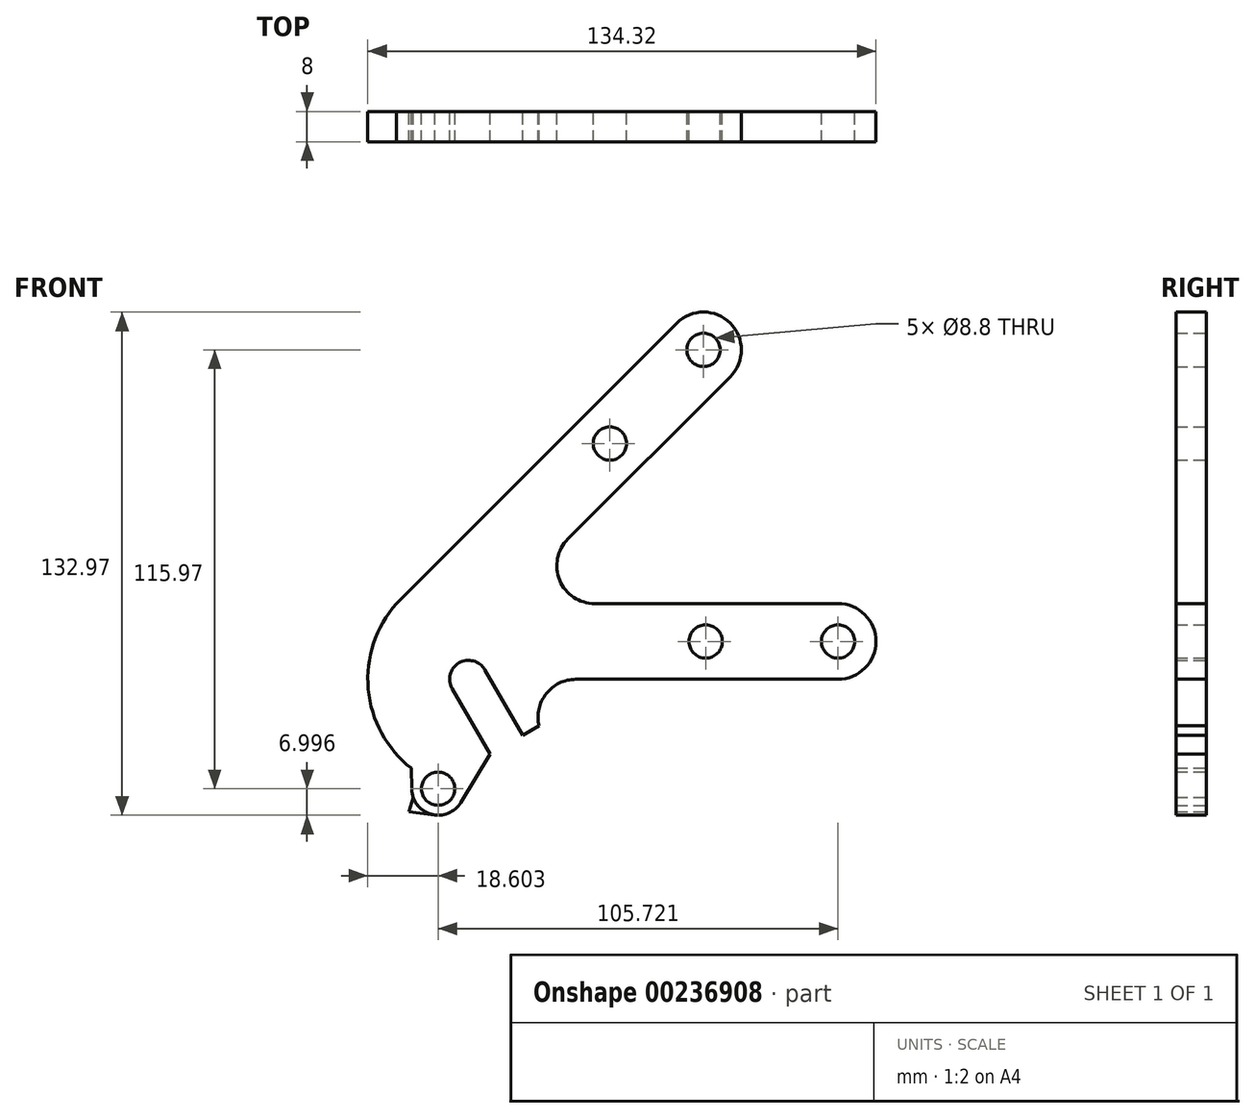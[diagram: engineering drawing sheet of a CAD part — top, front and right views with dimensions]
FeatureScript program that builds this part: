
annotation { "Feature Type Name" : "Feature", "Feature Type Description" : "" }
export const myFeature = defineFeature(function(context is Context, id is Id, definition is map)
    precondition{}
    {
        {
            var Q0;
            Q0=qCreatedBy(makeId("Front.planeOp"),FACE);
            var sketch = newSketch(context, id + "F0", { "sketchPlane" : qUnion([Q0])});
            skLineSegment(sketch, "E0", {"start": v(-20.18, 0) * mm, "end": v(-273.76, 0) * mm, "construction": true});
            skLineSegment(sketch, "E1", {"start": v(-273.76, 0) * mm, "end": v(-273.76, 78.06) * mm, "construction": true});
            skCircle(sketch, "E2", {"center": v(-273.76, 0) * mm, "radius": 5 * mm});
            skLineSegment(sketch, "E3", {"start": v(-273.76, 0) * mm, "end": v(-323.6, 0) * mm, "construction": true});
            skLineSegment(sketch, "E4", {"start": v(-323.6, 0) * mm, "end": v(-285.45, 38.15) * mm, "construction": true});
            skLineSegment(sketch, "E5", {"start": v(-285.45, 38.15) * mm, "end": v(-249.39, 74.21) * mm, "construction": true});
            skLineSegment(sketch, "E6", {"start": v(-249.39, 74.21) * mm, "end": v(-273.76, 0) * mm, "construction": true});
            skLineSegment(sketch, "E7", {"start": v(-285.45, 38.15) * mm, "end": v(-273.76, 0) * mm, "construction": true});
            skLineSegment(sketch, "E8", {"start": v(-273.76, 0) * mm, "end": v(-273.76, -28.91) * mm, "construction": true});
            skLineSegment(sketch, "E9", {"start": v(-273.76, -28.91) * mm, "end": v(-281.76, -28.91) * mm, "construction": true});
            skLineSegment(sketch, "E10", {"start": v(-281.76, -28.91) * mm, "end": v(-273.76, 0) * mm, "construction": true});
            skCircle(sketch, "E11", {"center": v(-281.76, -28.91) * mm, "radius": 4 * mm});
            skLineSegment(sketch, "E12", {"start": v(-273.76, 0) * mm, "end": v(-263.76, -17.32) * mm, "construction": true});
            skCircle(sketch, "E13", {"center": v(-263.76, -17.32) * mm, "radius": 5 * mm});
            skLineSegment(sketch, "E14", {"start": v(-259.43, -14.82) * mm, "end": v(-269.43, 2.5) * mm});
            skLineSegment(sketch, "E15", {"start": v(-268.09, -19.82) * mm, "end": v(-278.09, -2.5) * mm});
            skCircle(sketch, "E16", {"center": v(-281.76, -28.91) * mm, "radius": 7 * mm});
            skLineSegment(sketch, "E17", {"start": v(-288.38, -31.18) * mm, "end": v(-289.45, -35.04) * mm});
            skLineSegment(sketch, "E18", {"start": v(-289.45, -35.04) * mm, "end": v(-282.6, -35.86) * mm});
            skLineSegment(sketch, "E19", {"start": v(-268.09, -19.82) * mm, "end": v(-275.77, -32.53) * mm});
            skCircle(sketch, "E20", {"center": v(-285.45, 38.15) * mm, "radius": 5 * mm});
            skCircle(sketch, "E21", {"center": v(-249.39, 74.21) * mm, "radius": 5 * mm});
            skLineSegment(sketch, "E22", {"start": v(-290.45, 38.02) * mm, "end": v(-288.75, -29.1) * mm});
            skLineSegment(sketch, "E23", {"start": v(-281.91, 41.68) * mm, "end": v(-252.92, 70.68) * mm});
            skLineSegment(sketch, "E24", {"start": v(-261.57, 37.1) * mm, "end": v(-202.28, 96.4) * mm, "construction": true});
            skLineSegment(sketch, "E25", {"start": v(-153.76, 0) * mm, "end": v(-153.76, 35.52) * mm, "construction": true});
            skLineSegment(sketch, "E26", {"start": v(-269.43, 2.5) * mm, "end": v(-244.67, 72.54) * mm});
            skCircle(sketch, "E27", {"center": v(-273.76, 0) * mm, "radius": 30 * mm});
            skSolve(sketch);
        }
        {
            var Q0;
            Q0=qCreatedBy(makeId("Front.planeOp"),FACE);
            var sketch = newSketch(context, id + "F1", { "sketchPlane" : qUnion([Q0])});
            skCircle(sketch, "E28", {"center": v(-176.04, 10) * mm, "radius": 10 * mm});
            skCircle(sketch, "E29", {"center": v(-211.62, 87.06) * mm, "radius": 10 * mm});
            skCircle(sketch, "E30", {"center": v(-273.76, 0) * mm, "radius": 10 * mm});
            skCircle(sketch, "E31", {"center": v(-263.76, -17.32) * mm, "radius": 10 * mm});
            skLineSegment(sketch, "E32", {"start": v(-265.1, 5) * mm, "end": v(-255.1, -12.32) * mm});
            skLineSegment(sketch, "E33", {"start": v(-255.1, -12.32) * mm, "end": v(-272.42, -22.32) * mm});
            skLineSegment(sketch, "E34", {"start": v(-273.76, 0) * mm, "end": v(-176.04, 0) * mm});
            skLineSegment(sketch, "E35", {"start": v(-306.67, -22.14) * mm, "end": v(-204.55, 79.98) * mm});
            skLineSegment(sketch, "E36", {"start": v(-351.95, 20) * mm, "end": v(-176.04, 20) * mm});
            skLineSegment(sketch, "E37", {"start": v(-218.7, 94.13) * mm, "end": v(-344.78, -31.96) * mm});
            skCircle(sketch, "E38", {"center": v(-285.45, 38.15) * mm, "radius": 5 * mm});
            skCircle(sketch, "E39", {"center": v(-249.39, 74.21) * mm, "radius": 5 * mm});
            skLineSegment(sketch, "E40", {"start": v(-285.45, 38.15) * mm, "end": v(-280.06, 32.76) * mm, "construction": true});
            skLineSegment(sketch, "E41", {"start": v(-249.39, 74.21) * mm, "end": v(-244, 68.82) * mm, "construction": true});
            skLineSegment(sketch, "E42", {"start": v(-290.28, 36.85) * mm, "end": v(-287.25, 25.57) * mm});
            skLineSegment(sketch, "E43.MirrorCS", {"start": v(-284.16, 42.98) * mm, "end": v(-272.87, 39.95) * mm});
            skLineSegment(sketch, "E44", {"start": v(-254.22, 72.92) * mm, "end": v(-251.2, 61.63) * mm});
            skLineSegment(sketch, "E45.MirrorCS", {"start": v(-248.1, 79.04) * mm, "end": v(-236.8, 76.02) * mm});
            skCircle(sketch, "E46", {"center": v(-240.4, 30) * mm, "radius": 10 * mm});
            skCircle(sketch, "E47", {"center": v(-245.37, -10) * mm, "radius": 10 * mm});
            skLineSegment(sketch, "E48", {"start": v(-176.04, 10) * mm, "end": v(-211.04, 10) * mm, "construction": true});
            skLineSegment(sketch, "E49", {"start": v(-211.62, 87.06) * mm, "end": v(-236.37, 62.3) * mm, "construction": true});
            skArc(sketch, "E50", {"start": v(-292.82, 20) * mm, "mid": v(-300.24, -2.59) * mm, "end": v(-288.9, -23.48) * mm});
            skCircle(sketch, "E51", {"center": v(-281.76, -28.91) * mm, "radius": 7 * mm});
            skLineSegment(sketch, "E52", {"start": v(-288.9, -23.48) * mm, "end": v(-288.75, -29.1) * mm});
            skLineSegment(sketch, "E53", {"start": v(-275.77, -32.53) * mm, "end": v(-268.09, -19.82) * mm});
            skSolve(sketch);
        }
        {
            var Q0;
            {var subQ0=sQuery(id+"F1.wireOp",EDGE,"E28");var subQ1=makeQuery(id+"F1.imprint","INTERSECT",VERTEX,{"derivedFrom":[subQ0,sQuery(id+"F1.wireOp",EDGE,"E34")]});Q0=makeQuery(id+"F1.imprint","IMPRINT",FACE,{"disambiguationData":[TD([[makeQuery(id+"F1.imprint","IMPRINT",EDGE,{"disambiguationData":[TD([[subQ1,1.0]])],"derivedFrom":subQ0}),1.0]])]});}
            var Q1;
            {var subQ0=sQuery(id+"F1.wireOp",EDGE,"E34");var subQ8=sQuery(id+"F1.wireOp",EDGE,"E28");var subQ9=makeQuery(id+"F1.imprint","INTERSECT",VERTEX,{"derivedFrom":[subQ8,subQ0]});Q1=makeQuery(id+"F1.imprint","IMPRINT",FACE,{"disambiguationData":[TD([[makeQuery(id+"F1.imprint","IMPRINT",EDGE,{"disambiguationData":[TD([[subQ9,1.0]])],"derivedFrom":subQ8}),-1.0]])]});}
            var Q2;
            {var subQ0=sQuery(id+"F1.wireOp",EDGE,"E47");var subQ3=sQuery(id+"F1.wireOp",EDGE,"E34");var subQ5=makeQuery(id+"F1.imprint","INTERSECT",VERTEX,{"derivedFrom":[subQ3,subQ0]});Q2=makeQuery(id+"F1.imprint","IMPRINT",FACE,{"disambiguationData":[TD([[makeQuery(id+"F1.imprint","IMPRINT",EDGE,{"disambiguationData":[TD([[subQ5,1.0]])],"derivedFrom":subQ3}),-1.0]])]});}
            var Q3;
            {var subQ0=sQuery(id+"F1.wireOp",EDGE,"E34");var subQ1=sQuery(id+"F1.wireOp",EDGE,"E30");var subQ2=makeQuery(id+"F1.imprint","INTERSECT",VERTEX,{"derivedFrom":[subQ1,subQ0]});Q3=makeQuery(id+"F1.imprint","IMPRINT",FACE,{"disambiguationData":[TD([[makeQuery(id+"F1.imprint","IMPRINT",EDGE,{"disambiguationData":[TD([[subQ2,1.0]])],"derivedFrom":subQ1}),-1.0]])]});}
            var Q4;
            {var subQ0=sQuery(id+"F1.wireOp",EDGE,"E33");var subQ1=sQuery(id+"F1.wireOp",EDGE,"E31");var subQ4=makeQuery(id+"F1.imprint","INTERSECT",VERTEX,{"derivedFrom":[subQ1,subQ0]});Q4=makeQuery(id+"F1.imprint","IMPRINT",FACE,{"disambiguationData":[TD([[makeQuery(id+"F1.imprint","IMPRINT",EDGE,{"disambiguationData":[TD([[subQ4,1.0]])],"derivedFrom":subQ1}),1.0]])]});}
            var Q5;
            {var subQ0=sQuery(id+"F1.wireOp",EDGE,"E33");var subQ1=sQuery(id+"F1.wireOp",EDGE,"E31");var subQ2=makeQuery(id+"F1.imprint","INTERSECT",VERTEX,{"derivedFrom":[subQ1,subQ0]});Q5=makeQuery(id+"F1.imprint","IMPRINT",FACE,{"disambiguationData":[TD([[makeQuery(id+"F1.imprint","IMPRINT",EDGE,{"disambiguationData":[TD([[subQ2,-1.0]])],"derivedFrom":subQ1}),1.0]])]});}
            var Q6;
            {var subQ12=sQuery(id+"F1.wireOp",EDGE,"E52");Q6=makeQuery(id+"F1.imprint","IMPRINT",FACE,{"disambiguationData":[TD([[makeQuery(id+"F1.imprint","IMPRINT",EDGE,{"derivedFrom":subQ12}),1.0]])]});}
            var Q7;
            {var subQ0=sQuery(id+"F1.wireOp",EDGE,"E51");var subQ1=makeQuery(id+"F1.imprint","INTERSECT",VERTEX,{"derivedFrom":[subQ0,sQuery(id+"F1.wireOp",EDGE,"E52")]});Q7=makeQuery(id+"F1.imprint","IMPRINT",FACE,{"disambiguationData":[TD([[makeQuery(id+"F1.imprint","IMPRINT",EDGE,{"disambiguationData":[TD([[subQ1,-1.0]])],"derivedFrom":subQ0}),1.0]])]});}
            var Q8;
            {var subQ0=sQuery(id+"F1.wireOp",EDGE,"E30");var subQ5=makeQuery(id+"F1.imprint","INTERSECT",VERTEX,{"derivedFrom":[subQ0,sQuery(id+"F1.wireOp",EDGE,"E32")]});Q8=makeQuery(id+"F1.imprint","IMPRINT",FACE,{"disambiguationData":[TD([[makeQuery(id+"F1.imprint","IMPRINT",EDGE,{"disambiguationData":[TD([[subQ5,1.0]])],"derivedFrom":subQ0}),1.0]])]});}
            var Q9;
            {var subQ0=sQuery(id+"F1.wireOp",EDGE,"E35");var subQ1=sQuery(id+"F1.wireOp",EDGE,"E30");var subQ2=makeQuery(id+"F1.imprint","INTERSECT",VERTEX,{"disambiguationData":[OD(0.0)],"derivedFrom":[subQ1,subQ0]});Q9=makeQuery(id+"F1.imprint","IMPRINT",FACE,{"disambiguationData":[TD([[makeQuery(id+"F1.imprint","IMPRINT",EDGE,{"disambiguationData":[TD([[subQ2,-1.0]])],"derivedFrom":subQ1}),1.0]])]});}
            var Q10;
            {var subQ3=sQuery(id+"F1.wireOp",EDGE,"E35");var subQ6=sQuery(id+"F1.wireOp",EDGE,"E30");var subQ8=makeQuery(id+"F1.imprint","INTERSECT",VERTEX,{"disambiguationData":[OD(0.0)],"derivedFrom":[subQ6,subQ3]});Q10=makeQuery(id+"F1.imprint","IMPRINT",FACE,{"disambiguationData":[TD([[makeQuery(id+"F1.imprint","IMPRINT",EDGE,{"disambiguationData":[TD([[subQ8,-1.0]])],"derivedFrom":subQ6}),-1.0]])]});}
            var Q11;
            {var subQ0=sQuery(id+"F1.wireOp",EDGE,"E35");var subQ1=sQuery(id+"F1.wireOp",EDGE,"E29");var subQ2=makeQuery(id+"F1.imprint","INTERSECT",VERTEX,{"derivedFrom":[subQ1,subQ0]});Q11=makeQuery(id+"F1.imprint","IMPRINT",FACE,{"disambiguationData":[TD([[makeQuery(id+"F1.imprint","IMPRINT",EDGE,{"disambiguationData":[TD([[subQ2,1.0]])],"derivedFrom":subQ1}),-1.0]])]});}
            var Q12;
            {var subQ0=sQuery(id+"F1.wireOp",EDGE,"E46");var subQ1=sQuery(id+"F1.wireOp",EDGE,"E35");var subQ2=makeQuery(id+"F1.imprint","INTERSECT",VERTEX,{"derivedFrom":[subQ1,subQ0]});Q12=makeQuery(id+"F1.imprint","IMPRINT",FACE,{"disambiguationData":[TD([[makeQuery(id+"F1.imprint","IMPRINT",EDGE,{"disambiguationData":[TD([[subQ2,1.0]])],"derivedFrom":subQ1}),-1.0]])]});}
            var Q13;
            {var subQ0=sQuery(id+"F1.wireOp",EDGE,"E29");var subQ1=makeQuery(id+"F1.imprint","INTERSECT",VERTEX,{"derivedFrom":[subQ0,sQuery(id+"F1.wireOp",EDGE,"E35")]});Q13=makeQuery(id+"F1.imprint","IMPRINT",FACE,{"disambiguationData":[TD([[makeQuery(id+"F1.imprint","IMPRINT",EDGE,{"disambiguationData":[TD([[subQ1,1.0]])],"derivedFrom":subQ0}),1.0]])]});}
            var Q14;
            {var subQ0=sQuery(id+"F1.wireOp",EDGE,"E32");var subQ1=sQuery(id+"F1.wireOp",EDGE,"E30");var subQ2=makeQuery(id+"F1.imprint","INTERSECT",VERTEX,{"derivedFrom":[subQ1,subQ0]});Q14=makeQuery(id+"F1.imprint","IMPRINT",FACE,{"disambiguationData":[TD([[makeQuery(id+"F1.imprint","IMPRINT",EDGE,{"disambiguationData":[TD([[subQ2,1.0]])],"derivedFrom":subQ1}),-1.0]])]});}
            var Q15;
            {var subQ0=sQuery(id+"F0.wireOp",EDGE,"E17");Q15=makeQuery(id+"F0.imprint","IMPRINT",FACE,{"disambiguationData":[TD([[makeQuery(id+"F0.imprint","IMPRINT",EDGE,{"derivedFrom":subQ0}),1.0]])]});}
            extrude(context, id + "F2", {"entities" : qUnion([Q0, Q1, Q2, Q3, Q4, Q5, Q6, Q7, Q8, Q9, Q10, Q11, Q12, Q13, Q14, Q15]), "depth" : 8 * mm});
        }
        {
            var Q0;
            {var subQ0=sQuery(id+"F0.wireOp",EDGE,"E2");var subQ2=makeQuery(id+"F0.imprint","INTERSECT",VERTEX,{"derivedFrom":[subQ0,sQuery(id+"F0.wireOp",EDGE,"E15")]});Q0=makeQuery(id+"F0.imprint","IMPRINT",FACE,{"disambiguationData":[TD([[makeQuery(id+"F0.imprint","IMPRINT",EDGE,{"disambiguationData":[TD([[subQ2,1.0]])],"derivedFrom":subQ0}),1.0]])]});}
            var Q1;
            {var subQ0=sQuery(id+"F0.wireOp",EDGE,"E14");Q1=makeQuery(id+"F0.imprint","IMPRINT",FACE,{"disambiguationData":[TD([[makeQuery(id+"F0.imprint","IMPRINT",EDGE,{"derivedFrom":subQ0}),1.0]])]});}
            var Q2;
            {var subQ0=sQuery(id+"F0.wireOp",EDGE,"E13");var subQ1=makeQuery(id+"F0.imprint","INTERSECT",VERTEX,{"derivedFrom":[subQ0,sQuery(id+"F0.wireOp",EDGE,"E14")]});Q2=makeQuery(id+"F0.imprint","IMPRINT",FACE,{"disambiguationData":[TD([[makeQuery(id+"F0.imprint","IMPRINT",EDGE,{"disambiguationData":[TD([[subQ1,-1.0]])],"derivedFrom":subQ0}),1.0]])]});}
            extrude(context, id + "F3", {"entities" : qUnion([Q0, Q1, Q2]), "operationType" : NewBodyOperationType.REMOVE, "endBound" : BoundingType.UP_TO_NEXT, "depth" : 25 * mm});
        }
        {
            var Q0;
            Q0=sQuery(id+"F1.wireOp",VERTEX,"E49.end");
            var Q1;
            Q1=sQuery(id+"F1.wireOp",VERTEX,"E49.start");
            var Q2;
            Q2=sQuery(id+"F1.wireOp",VERTEX,"E28.center");
            var Q3;
            Q3=sQuery(id+"F1.wireOp",VERTEX,"E48.end");
            var Q4;
            Q4=makeQuery(id+"F2.opExtrude","SWEPT_BODY",BODY,{"disambiguationData":[OSD([sQuery(id+"F1.wireOp",EDGE,"E28"),sQuery(id+"F1.wireOp",EDGE,"E29"),sQuery(id+"F1.wireOp",EDGE,"E33"),sQuery(id+"F1.wireOp",EDGE,"E34"),sQuery(id+"F1.wireOp",EDGE,"E35"),sQuery(id+"F1.wireOp",EDGE,"E36"),sQuery(id+"F1.wireOp",EDGE,"E37"),sQuery(id+"F1.wireOp",EDGE,"E46"),sQuery(id+"F1.wireOp",EDGE,"E47"),sQuery(id+"F1.wireOp",EDGE,"E50"),sQuery(id+"F1.wireOp",EDGE,"E51"),sQuery(id+"F1.wireOp",EDGE,"E52"),sQuery(id+"F1.wireOp",EDGE,"E53")])]});
            hole(context, id + "F4", {"style" : HoleStyle.SIMPLE, "endStyle" : HoleEndStyle.THROUGH, "oppositeDirection" : true, "standardTappedOrClearance" : lookupTablePath({ "standard" : "ISO", "fit" : "Normal", "size" : "M8", "type" : "Clearance" }), "standardBlindInLast" : lookupTablePath({ "fit" : "Standard", "standard" : "ISO", "size" : "M8", "type" : "Clearance" }), "holeDiameter" : 8.8 * mm, "locations" : qUnion([Q0, Q1, Q2, Q3]), "scope" : qUnion([Q4]), "isTappedThrough" : true});
        }
        {
            var Q0;
            Q0=sQuery(id+"F1.wireOp",VERTEX,"E51.center");
            var Q1;
            Q1=makeQuery(id+"F2.opExtrude","SWEPT_BODY",BODY,{"disambiguationData":[OSD([sQuery(id+"F1.wireOp",EDGE,"E28"),sQuery(id+"F1.wireOp",EDGE,"E29"),sQuery(id+"F1.wireOp",EDGE,"E33"),sQuery(id+"F1.wireOp",EDGE,"E34"),sQuery(id+"F1.wireOp",EDGE,"E35"),sQuery(id+"F1.wireOp",EDGE,"E36"),sQuery(id+"F1.wireOp",EDGE,"E37"),sQuery(id+"F1.wireOp",EDGE,"E46"),sQuery(id+"F1.wireOp",EDGE,"E47"),sQuery(id+"F1.wireOp",EDGE,"E50"),sQuery(id+"F1.wireOp",EDGE,"E51"),sQuery(id+"F1.wireOp",EDGE,"E52"),sQuery(id+"F1.wireOp",EDGE,"E53")])]});
            hole(context, id + "F5", {"style" : HoleStyle.SIMPLE, "endStyle" : HoleEndStyle.THROUGH, "oppositeDirection" : true, "standardTappedOrClearance" : lookupTablePath({ "standard" : "ISO", "fit" : "Normal", "size" : "M8", "type" : "Clearance" }), "standardBlindInLast" : lookupTablePath({ "fit" : "Standard", "standard" : "ISO", "size" : "M8", "type" : "Clearance" }), "holeDiameter" : 8.8 * mm, "locations" : qUnion([Q0]), "scope" : qUnion([Q1]), "isTappedThrough" : true});
        }
    });
